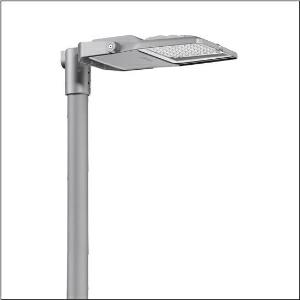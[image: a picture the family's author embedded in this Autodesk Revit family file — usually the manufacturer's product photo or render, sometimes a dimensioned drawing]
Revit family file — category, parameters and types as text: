
# Revit family: floodlight_fl_21_iq_mini___pl61_5xa7771b2c3a_a4a3
name_source: partatom
category: Lighting Fixtures
units: mm (PartAtom-declared; Revit-internal decimal feet)

## family parameters
Cut with Voids When Loaded = No
Host = Face
Light Source = No
Part Type = Normal
Room Calculation Point = No
Round Connector Dimension = Use Diameter
Shared = No

## types (1)
- --- (1 x LED, 6120 lm, 45.5 W, 3000K)
    Apparent Load = 46 VA
    CIE Flux Codes = 33 65 98 100 100
    Color Rendering = 70
    Color Temperature = 3000K
    Default Elevation = 1800 mm
    Description = Floodlight FL 21 iQ mini, floodlight, primary light control with lens, of PMMA, primary optical cover: protective disc, of toughened safety glass, transparent, light distribution: PL61, light emission: direct distribution, installation type: surface-mounted, LED, High Power LED, rated luminous flux: 6.120lm, luminous efficacy: 135lm/W, light colour: 730, colour temperature: 3000K, control: Auto-Match, Temp-Guard, Lumen-Switch, Night-Set, Smart-Wire, Light-Fading, Desk-Remote (wireless, voltage-free reading and setting of iQ features in the workshop via application-optimized NFC function/RFID function), optimised constant luminous flux control (CLO 2.0), with terminal, 6-pole, mains connection: 220..240V, AC, 50/60Hz, start of lifetime: 46W, end of service life: 48W, reduction: 22W, luminaire housing, of diecast aluminium, powder-coated, Siteco® metallic grey (DB 702S), corrosivity category C5 mid according to DIN EN ISO 12944, sealing non-destructively replaceable, please order mast flange separately, mast bracket, of steel, galvanised, powder-coated, Siteco® metallic grey (DB 702S), protection rating (complete): IP66, insulation class (complete): insulation class II (safety insulation), certification: CE, ENEC, VDE, protection symbol: D, impact resistance: IK08, permissible operating ambient temperature: -40..+40°C, permissible operating ambient temperature for outdoor applications: -40..+50°C, standard: DIN EN 12944, LABS conformity tested according to VDMA 24364:2018-05, packaging unit: 1 piece

Light Distribution: PL61
    Height = 70 mm
    Lamp = 1 x LED
    Lamp Light Flux = 6120 lm
    Lamp Power = 45.5 W
    Lamp count = 1
    Length = 485 mm
    Luminous efficacy = 135 lm/W
    Manufacturer = Siteco
    ModVariant = No
    Model = 5XA7771B2C3A
    Number of Poles = 1
    OnlyDefault = Yes
    Power Factor = 1
    Product Name = Floodlight FL 21 iQ mini | PL61
    Product group = floodlight | pylon annexe
    ProductGroupID = 6200
    Protection Class = Protection class II
    Protection Degree = IP 66
    RLX_Detail_Level = 1
    RLX_Emergency_Light_Flux = 0 lm
    RLX_Emergency_Type = 0
    RLX_Emergency_Type_DB = No
    RlxData = <blob elided: 101197 chars, md5=ad5f988c>
    Socket = socket
    Standby Power = 0 W
    System Light Flux = 6120 lm
    System Power = 46 W
    Type Comments = factory setting: luminous flux: 100 % | dim-lin: 254 | 463 mA
    Type Image = l_1007125.jpg
    URL = http://relux.com
    VarID = @adj_124763
    Voltage = 0 V
    Weight = 0.00 kg
    Width = 337 mm

## geometry (parser evidence)
native form markers: Blend x4, Sweep x13
no freeform markers — native parametric forms only
